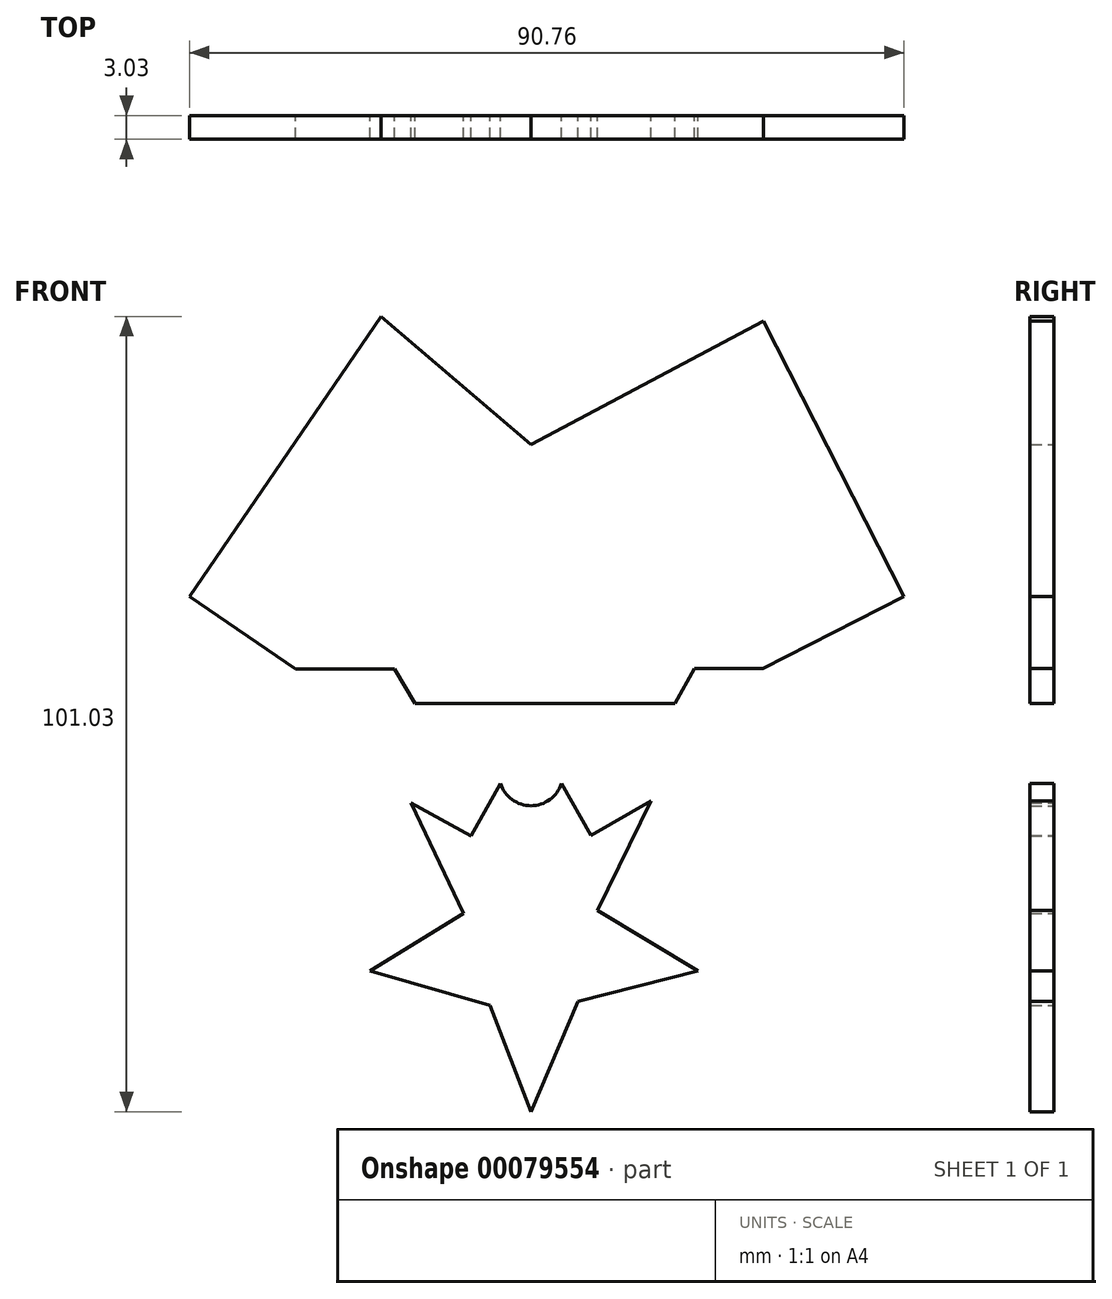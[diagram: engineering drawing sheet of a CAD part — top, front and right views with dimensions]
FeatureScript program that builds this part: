
annotation { "Feature Type Name" : "Feature", "Feature Type Description" : "" }
export const myFeature = defineFeature(function(context is Context, id is Id, definition is map)
    precondition{}
    {
        {
            var Q0;
            Q0=qCreatedBy(makeId("Front.planeOp"),FACE);
            var sketch = newSketch(context, id + "F0", { "sketchPlane" : qUnion([Q0])});
            skCircle(sketch, "E0", {"center": v(0, 0) * mm, "radius": 9.42 * mm});
            skCircle(sketch, "E1", {"center": v(0, 0) * mm, "radius": 8.83 * mm});
            skLineSegment(sketch, "E2", {"start": v(-5.22, -7.84) * mm, "end": v(0, -21.35) * mm});
            skLineSegment(sketch, "E3", {"start": v(0, -21.35) * mm, "end": v(5.94, -7.31) * mm});
            skLineSegment(sketch, "E4", {"start": v(0, 9.42) * mm, "end": v(15.24, 18.12) * mm});
            skLineSegment(sketch, "E5", {"start": v(15.24, 18.12) * mm, "end": v(8.44, 4.2) * mm});
            skLineSegment(sketch, "E6", {"start": v(8.44, 4.2) * mm, "end": v(21.18, -3.44) * mm});
            skLineSegment(sketch, "E7", {"start": v(21.18, -3.44) * mm, "end": v(5.94, -7.31) * mm});
            skLineSegment(sketch, "E8", {"start": v(0, 9.42) * mm, "end": v(-15.24, 17.89) * mm});
            skLineSegment(sketch, "E9", {"start": v(-15.24, 17.89) * mm, "end": v(-8.61, 3.82) * mm});
            skLineSegment(sketch, "E10", {"start": v(-8.61, 3.82) * mm, "end": v(-20.46, -3.44) * mm});
            skLineSegment(sketch, "E11", {"start": v(-20.46, -3.44) * mm, "end": v(-5.22, -7.84) * mm});
            skLineSegment(sketch, "E12", {"start": v(-7.62, 13.65) * mm, "end": v(-3.9, 20.33) * mm});
            skLineSegment(sketch, "E13", {"start": v(7.62, 13.77) * mm, "end": v(3.85, 20.33) * mm});
            skArc(sketch, "E14", {"start": v(-3.9, 20.33) * mm, "mid": v(-0.03, 17.52) * mm, "end": v(3.85, 20.33) * mm});
            skLineSegment(sketch, "E15", {"start": v(-0.03, 17.52) * mm, "end": v(-0.03, 24.25) * mm});
            skLineSegment(sketch, "E16", {"start": v(18.24, 30.51) * mm, "end": v(-14.78, 30.51) * mm});
            skArc(sketch, "E17", {"start": v(-9.45, 30.51) * mm, "mid": v(-5.71, 25.92) * mm, "end": v(-0.03, 24.25) * mm});
            skLineSegment(sketch, "E18", {"start": v(18.24, 30.51) * mm, "end": v(23.2, 39.38) * mm});
            skLineSegment(sketch, "E19", {"start": v(23.2, 39.38) * mm, "end": v(23.2, 54.62) * mm});
            skLineSegment(sketch, "E20", {"start": v(23.2, 54.62) * mm, "end": v(18.09, 63.4) * mm});
            skLineSegment(sketch, "E21", {"start": v(18.09, 63.4) * mm, "end": v(-14.93, 63.4) * mm});
            skLineSegment(sketch, "E22", {"start": v(-14.93, 63.4) * mm, "end": v(-19.9, 54.53) * mm});
            skLineSegment(sketch, "E23", {"start": v(-19.9, 54.53) * mm, "end": v(-19.9, 39.29) * mm});
            skLineSegment(sketch, "E24", {"start": v(-19.9, 39.29) * mm, "end": v(-14.78, 30.51) * mm});
            skLineSegment(sketch, "E25", {"start": v(18.24, 34.94) * mm, "end": v(29.47, 34.94) * mm});
            skPoint(sketch, "E25.startSnap0", {"position": v(20.73, 34.94) * mm});
            skLineSegment(sketch, "E26", {"start": v(29.47, 34.94) * mm, "end": v(47.37, 44.1) * mm});
            skLineSegment(sketch, "E27", {"start": v(47.37, 44.1) * mm, "end": v(29.49, 79.11) * mm});
            skLineSegment(sketch, "E28", {"start": v(-14.78, 34.9) * mm, "end": v(-29.96, 34.9) * mm});
            skPoint(sketch, "E28.startSnap0", {"position": v(-17.34, 34.9) * mm});
            skLineSegment(sketch, "E29", {"start": v(-29.96, 34.9) * mm, "end": v(-43.4, 44.1) * mm});
            skLineSegment(sketch, "E30", {"start": v(-43.4, 44.1) * mm, "end": v(-19.04, 79.68) * mm});
            skLineSegment(sketch, "E31", {"start": v(-19.04, 79.68) * mm, "end": v(0, 63.4) * mm});
            skLineSegment(sketch, "E32", {"start": v(0, 63.4) * mm, "end": v(29.49, 79.11) * mm});
            skSolve(sketch);
        }
        {
            var Q0;
            {var subQ4=sQuery(id+"F0.wireOp",EDGE,"E19");Q0=makeQuery(id+"F0.imprint","IMPRINT",FACE,{"disambiguationData":[TD([[makeQuery(id+"F0.imprint","IMPRINT",EDGE,{"derivedFrom":subQ4}),1.0]])]});}
            var Q1;
            {var subQ2=sQuery(id+"F0.wireOp",EDGE,"E10");Q1=makeQuery(id+"F0.imprint","IMPRINT",FACE,{"disambiguationData":[TD([[makeQuery(id+"F0.imprint","IMPRINT",EDGE,{"derivedFrom":subQ2}),1.0]])]});}
            var Q2;
            {var subQ0=sQuery(id+"F0.wireOp",EDGE,"E2");Q2=makeQuery(id+"F0.imprint","IMPRINT",FACE,{"disambiguationData":[TD([[makeQuery(id+"F0.imprint","IMPRINT",EDGE,{"derivedFrom":subQ0}),1.0]])]});}
            var Q3;
            {var subQ2=sQuery(id+"F0.wireOp",EDGE,"E6");Q3=makeQuery(id+"F0.imprint","IMPRINT",FACE,{"disambiguationData":[TD([[makeQuery(id+"F0.imprint","IMPRINT",EDGE,{"derivedFrom":subQ2}),-1.0]])]});}
            var Q4;
            {var subQ3=sQuery(id+"F0.wireOp",EDGE,"E19");Q4=makeQuery(id+"F0.imprint","IMPRINT",FACE,{"disambiguationData":[TD([[makeQuery(id+"F0.imprint","IMPRINT",EDGE,{"derivedFrom":subQ3}),-1.0]])]});}
            var Q5;
            {var subQ5=sQuery(id+"F0.wireOp",EDGE,"E22");Q5=makeQuery(id+"F0.imprint","IMPRINT",FACE,{"disambiguationData":[TD([[makeQuery(id+"F0.imprint","IMPRINT",EDGE,{"derivedFrom":subQ5}),-1.0]])]});}
            var Q6;
            {var subQ3=sQuery(id+"F0.wireOp",EDGE,"E5");Q6=makeQuery(id+"F0.imprint","IMPRINT",FACE,{"disambiguationData":[TD([[makeQuery(id+"F0.imprint","IMPRINT",EDGE,{"derivedFrom":subQ3}),-1.0]])]});}
            var Q7;
            {var subQ3=sQuery(id+"F0.wireOp",EDGE,"E9");Q7=makeQuery(id+"F0.imprint","IMPRINT",FACE,{"disambiguationData":[TD([[makeQuery(id+"F0.imprint","IMPRINT",EDGE,{"derivedFrom":subQ3}),1.0]])]});}
            var Q8;
            {var subQ1=sQuery(id+"F0.wireOp",EDGE,"E12");Q8=makeQuery(id+"F0.imprint","IMPRINT",FACE,{"disambiguationData":[TD([[makeQuery(id+"F0.imprint","IMPRINT",EDGE,{"derivedFrom":subQ1}),-1.0]])]});}
            var Q9;
            Q9=makeQuery(id+"F0.imprint","IMPRINT",FACE,{"disambiguationData":[TD([[makeQuery(id+"F0.imprint","IMPRINT",EDGE,{"derivedFrom":sQuery(id+"F0.wireOp",EDGE,"E1")}),-1.0]])]});
            var Q10;
            Q10=makeQuery(id+"F0.imprint","IMPRINT",FACE,{"disambiguationData":[TD([[makeQuery(id+"F0.imprint","IMPRINT",EDGE,{"derivedFrom":sQuery(id+"F0.wireOp",EDGE,"E1")}),1.0]])]});
            extrude(context, id + "F1", {"entities" : qUnion([Q0, Q1, Q2, Q3, Q4, Q5, Q6, Q7, Q8, Q9, Q10]), "depth" : 3.03 * mm});
        }
    });
